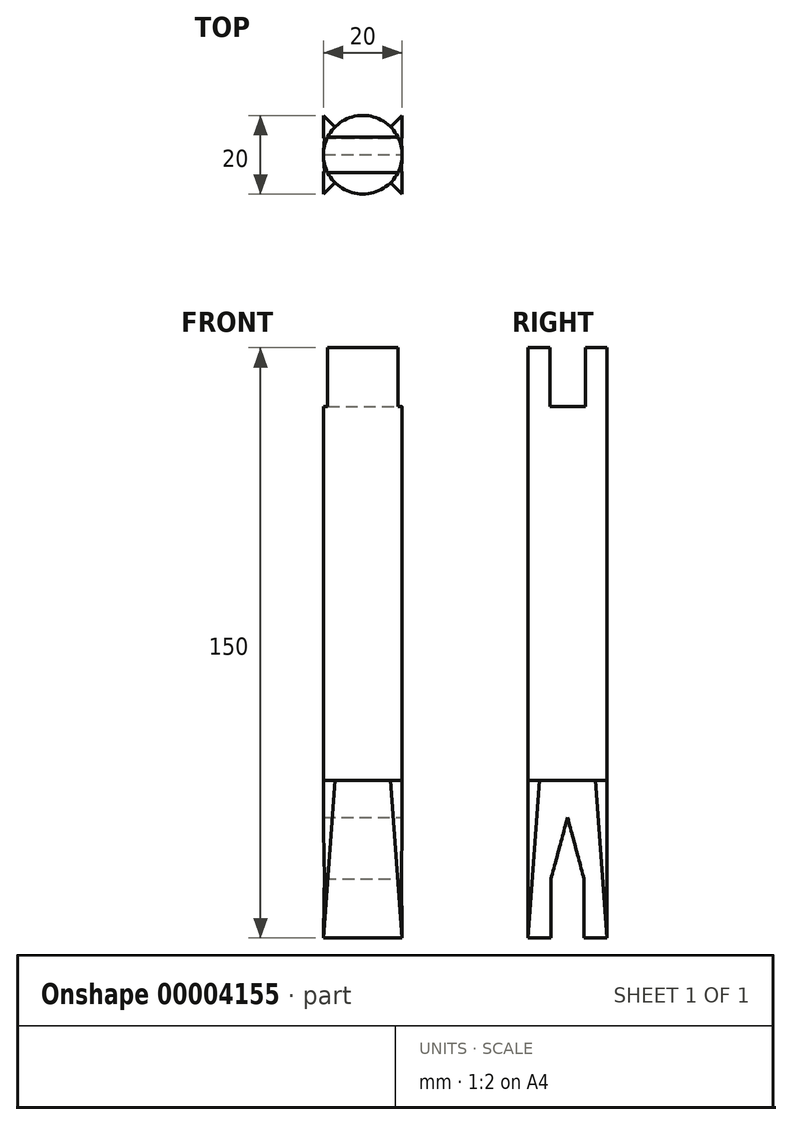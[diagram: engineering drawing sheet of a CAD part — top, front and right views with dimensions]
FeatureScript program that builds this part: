
annotation { "Feature Type Name" : "Feature", "Feature Type Description" : "" }
export const myFeature = defineFeature(function(context is Context, id is Id, definition is map)
    precondition{}
    {
        {
            var Q0;
            Q0=qCreatedBy(makeId("Top.planeOp"),FACE);
            var sketch = newSketch(context, id + "F0", { "sketchPlane" : qUnion([Q0])});
            skLineSegment(sketch, "E0.rect.bottom", {"start": v(-10, 10) * mm, "end": v(10, 10) * mm});
            skLineSegment(sketch, "E0.rect.top", {"start": v(-10, -10) * mm, "end": v(10, -10) * mm});
            skLineSegment(sketch, "E0.rect.left", {"start": v(-10, 10) * mm, "end": v(-10, -10) * mm});
            skLineSegment(sketch, "E0.rect.right", {"start": v(10, 10) * mm, "end": v(10, -10) * mm});
            skPoint(sketch, "E0.rect.middle", {"position": v(0, 0) * mm});
            skSolve(sketch);
        }
        {
            var Q0;
            Q0=qCreatedBy(makeId("Top.planeOp"),FACE);
            cPlane(context, id + "F1", {"entities" : qUnion([Q0]), "cplaneType" : CPlaneType.OFFSET, "offset" : 40 * mm, "width" : 150 * mm, "height" : 150 * mm});
        }
        {
            var Q0;
            Q0=qCreatedBy(id+"F1.planeOp",FACE);
            var sketch = newSketch(context, id + "F2", { "sketchPlane" : qUnion([Q0])});
            skCircle(sketch, "E1", {"center": v(0, 0) * mm, "radius": 10 * mm});
            skSolve(sketch);
        }
        {
            var Q0;
            Q0=makeQuery(id+"F0.imprint","IMPRINT",FACE,{"disambiguationData":[TD([[makeQuery(id+"F0.imprint","IMPRINT",EDGE,{"derivedFrom":sQuery(id+"F0.wireOp",EDGE,"E0.rect.bottom")}),-1.0]])]});
            var Q1;
            Q1=makeQuery(id+"F2.imprint","IMPRINT",FACE,{"disambiguationData":[TD([[makeQuery(id+"F2.imprint","IMPRINT",EDGE,{"derivedFrom":sQuery(id+"F2.wireOp",EDGE,"E1")}),1.0]])]});
            loft(context, id + "F3", {"sheetProfilesArray" : [{ "sheetProfileEntities" : qUnion([Q0]) }, { "sheetProfileEntities" : qUnion([Q1]) }]});
        }
        {
            var Q0;
            Q0=makeQuery(id+"F2.imprint","IMPRINT",FACE,{"disambiguationData":[TD([[makeQuery(id+"F2.imprint","IMPRINT",EDGE,{"derivedFrom":sQuery(id+"F2.wireOp",EDGE,"E1")}),1.0]])]});
            extrude(context, id + "F4", {"entities" : qUnion([Q0]), "operationType" : NewBodyOperationType.ADD, "depth" : 110 * mm});
        }
        {
            var Q0;
            Q0=qCreatedBy(makeId("Right.planeOp"),FACE);
            var sketch = newSketch(context, id + "F5", { "sketchPlane" : qUnion([Q0])});
            skLineSegment(sketch, "E2.rect.top", {"start": v(-4.2, -15) * mm, "end": v(4.2, -15) * mm});
            skLineSegment(sketch, "E2.rect.left", {"start": v(-4.2, 15) * mm, "end": v(-4.2, -15) * mm});
            skLineSegment(sketch, "E2.rect.right", {"start": v(4.2, 15) * mm, "end": v(4.2, -15) * mm});
            skPoint(sketch, "E2.rect.middle", {"position": v(0, 0) * mm});
            skLineSegment(sketch, "E3", {"start": v(0, 36.15) * mm, "end": v(0, -26.24) * mm, "construction": true});
            skLineSegment(sketch, "E4", {"start": v(4.2, 15) * mm, "end": v(0, 30.67) * mm});
            skLineSegment(sketch, "E5", {"start": v(14.13, 15) * mm, "end": v(-17.95, 15) * mm, "construction": true});
            skLineSegment(sketch, "E6.0.MirrorCS", {"start": v(-4.2, 15) * mm, "end": v(0, 30.67) * mm});
            skSolve(sketch);
        }
        {
            var Q0;
            Q0 = qSketchRegion(id + "F5", true);
            extrude(context, id + "F6", {"entities" : qUnion([Q0]), "operationType" : NewBodyOperationType.REMOVE, "endBound" : BoundingType.SYMMETRIC, "oppositeDirection" : true, "depth" : 25 * mm});
        }
        {
            var Q0;
            Q0=qCreatedBy(makeId("Right.planeOp"),FACE);
            var sketch = newSketch(context, id + "F7", { "sketchPlane" : qUnion([Q0])});
            skLineSegment(sketch, "E7", {"start": v(0, 148.34) * mm, "end": v(0, 73.5) * mm, "construction": true});
            skLineSegment(sketch, "E8.rect.bottom", {"start": v(-4.5, 165) * mm, "end": v(4.5, 165) * mm});
            skLineSegment(sketch, "E8.rect.top", {"start": v(-4.5, 135) * mm, "end": v(4.5, 135) * mm});
            skLineSegment(sketch, "E8.rect.left", {"start": v(-4.5, 165) * mm, "end": v(-4.5, 135) * mm});
            skLineSegment(sketch, "E8.rect.right", {"start": v(4.5, 165) * mm, "end": v(4.5, 135) * mm});
            skPoint(sketch, "E8.rect.middle", {"position": v(0, 150) * mm});
            skLineSegment(sketch, "E9.0", {"start": v(-10, 150) * mm, "end": v(10, 150) * mm});
            skSolve(sketch);
        }
        {
            var Q0;
            Q0 = qSketchRegion(id + "F7", true);
            extrude(context, id + "F8", {"entities" : qUnion([Q0]), "operationType" : NewBodyOperationType.REMOVE, "endBound" : BoundingType.SYMMETRIC, "oppositeDirection" : true, "depth" : 25 * mm});
        }
    });
